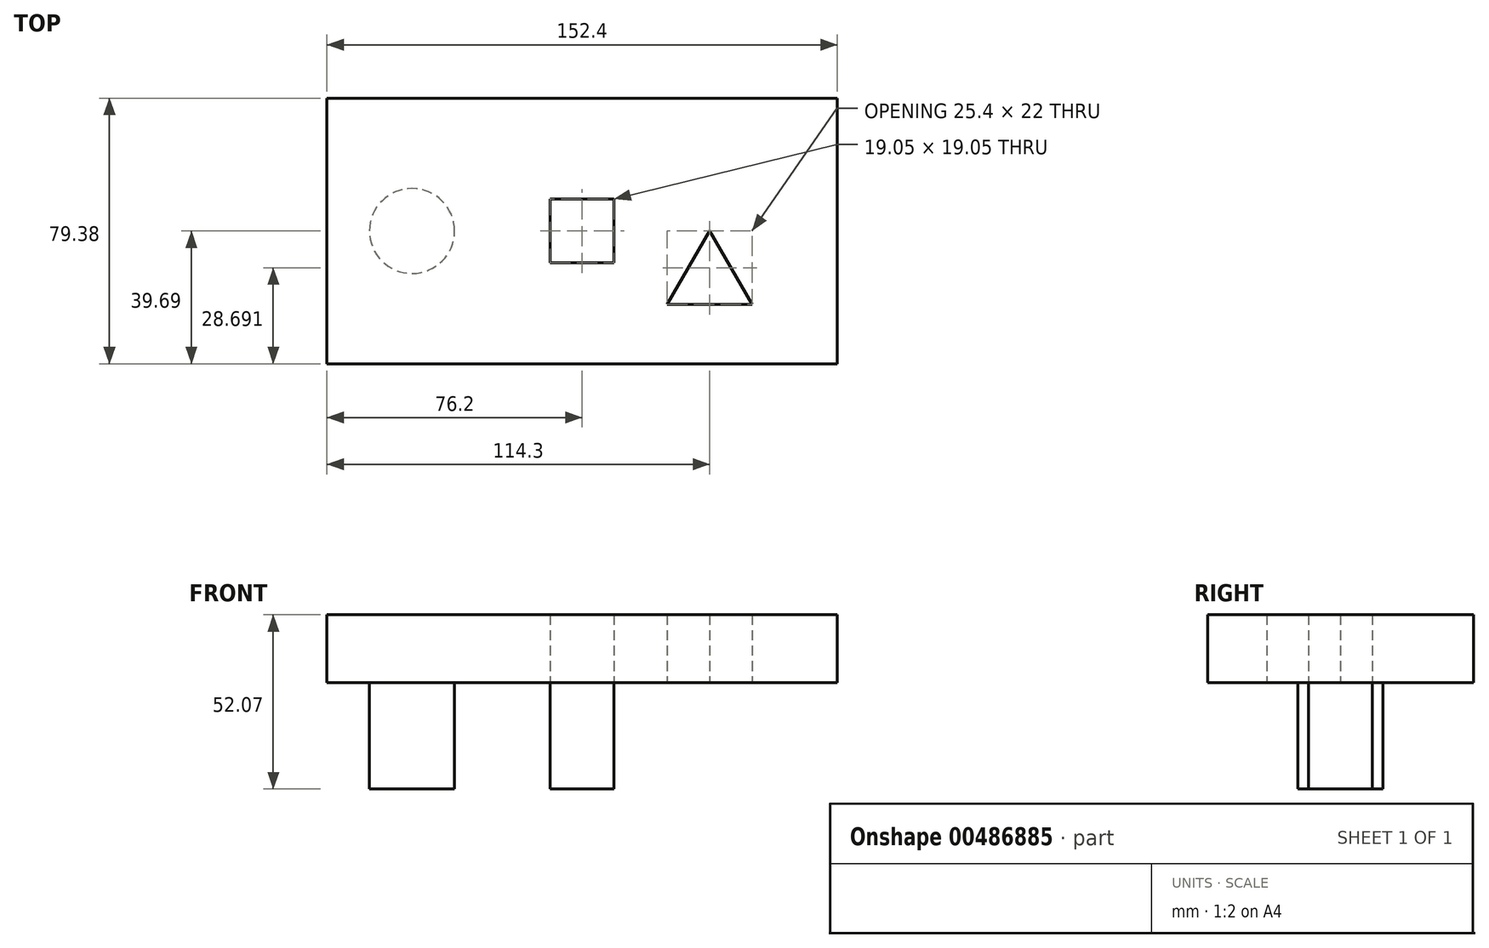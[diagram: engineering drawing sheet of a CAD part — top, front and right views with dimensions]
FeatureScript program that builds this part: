
annotation { "Feature Type Name" : "Feature", "Feature Type Description" : "" }
export const myFeature = defineFeature(function(context is Context, id is Id, definition is map)
    precondition{}
    {
        {
            var Q0;
            Q0=qCreatedBy(makeId("Top.planeOp"),FACE);
            var sketch = newSketch(context, id + "F0", { "sketchPlane" : qUnion([Q0])});
            skPoint(sketch, "E0", {"position": v(-31.75, 0) * mm});
            skLineSegment(sketch, "E1.bottom", {"start": v(-22.22, 9.53) * mm, "end": v(-41.27, 9.53) * mm});
            skLineSegment(sketch, "E1.top", {"start": v(-22.22, -9.52) * mm, "end": v(-41.27, -9.52) * mm});
            skLineSegment(sketch, "E1.left", {"start": v(-22.22, 9.53) * mm, "end": v(-22.22, -9.52) * mm});
            skLineSegment(sketch, "E1.right", {"start": v(-41.27, 9.53) * mm, "end": v(-41.27, -9.52) * mm});
            skCircle(sketch, "E2", {"center": v(-82.55, 0) * mm, "radius": 12.7 * mm});
            skLineSegment(sketch, "E3.bottom", {"start": v(44.45, -39.69) * mm, "end": v(-107.95, -39.69) * mm});
            skLineSegment(sketch, "E3.top", {"start": v(44.45, 39.69) * mm, "end": v(-107.95, 39.69) * mm});
            skLineSegment(sketch, "E3.left", {"start": v(44.45, -39.69) * mm, "end": v(44.45, 39.69) * mm});
            skLineSegment(sketch, "E3.right", {"start": v(-107.95, -39.69) * mm, "end": v(-107.95, 39.69) * mm});
            skPoint(sketch, "E4", {"position": v(44.45, 0) * mm});
            skPoint(sketch, "E5", {"position": v(6.35, 0) * mm});
            skLineSegment(sketch, "E6", {"start": v(6.35, 0) * mm, "end": v(-6.35, -22) * mm});
            skLineSegment(sketch, "E7", {"start": v(-6.35, -22) * mm, "end": v(19.05, -22) * mm});
            skLineSegment(sketch, "E8", {"start": v(19.05, -22) * mm, "end": v(6.35, 0) * mm});
            skSolve(sketch);
        }
        {
            var Q0;
            Q0=makeQuery(id+"F0.imprint","IMPRINT",FACE,{"disambiguationData":[TD([[makeQuery(id+"F0.imprint","IMPRINT",EDGE,{"derivedFrom":sQuery(id+"F0.wireOp",EDGE,"E1.bottom")}),-1.0]])]});
            var Q1;
            Q1=makeQuery(id+"F0.imprint","IMPRINT",FACE,{"disambiguationData":[TD([[makeQuery(id+"F0.imprint","IMPRINT",EDGE,{"derivedFrom":sQuery(id+"F0.wireOp",EDGE,"E2")}),1.0]])]});
            var Q2;
            Q2=makeQuery(id+"F0.imprint","IMPRINT",FACE,{"disambiguationData":[TD([[makeQuery(id+"F0.imprint","IMPRINT",EDGE,{"derivedFrom":sQuery(id+"F0.wireOp",EDGE,"1dAGqZZK-PbFe-BUMY-NSrG-KrEZ7z0RWpoe")}),1.0]])]});
            var Q3;
            Q3=makeQuery(id+"F0.imprint","IMPRINT",FACE,{"disambiguationData":[TD([[makeQuery(id+"F0.imprint","IMPRINT",EDGE,{"derivedFrom":sQuery(id+"F0.wireOp",EDGE,"LygEi8Ur-gzNw-TDgE-Le7G-bf86k6djG2GS")}),1.0]])]});
            var Q4;
            Q4=makeQuery(id+"F0.imprint","IMPRINT",FACE,{"disambiguationData":[TD([[makeQuery(id+"F0.imprint","IMPRINT",EDGE,{"derivedFrom":sQuery(id+"F0.wireOp",EDGE,"tCn7Srsb-gwfL-v9CE-pRFE-bM4LpM3Rr9z0")}),1.0]])]});
            var Q5;
            Q5=makeQuery(id+"F0.imprint","IMPRINT",FACE,{"disambiguationData":[TD([[makeQuery(id+"F0.imprint","IMPRINT",EDGE,{"derivedFrom":sQuery(id+"F0.wireOp",EDGE,"NWhCxObp-BHab-S6VO-F033-pommvVcIhDGg")}),1.0]])]});
            var Q6;
            Q6=makeQuery(id+"F0.imprint","IMPRINT",FACE,{"disambiguationData":[TD([[makeQuery(id+"F0.imprint","IMPRINT",EDGE,{"derivedFrom":sQuery(id+"F0.wireOp",EDGE,"Vu1bnHFe-H9mk-ZCjp-7Mg4-KF9IkP5c8JJK")}),1.0]])]});
            extrude(context, id + "F1", {"entities" : qUnion([Q0, Q1, Q2, Q3, Q4, Q5, Q6]), "depth" : 20.32 * mm});
        }
        {
            var Q0;
            Q0=makeQuery(id+"F0.imprint","IMPRINT",FACE,{"disambiguationData":[TD([[makeQuery(id+"F0.imprint","IMPRINT",EDGE,{"derivedFrom":sQuery(id+"F0.wireOp",EDGE,"E2")}),1.0]])]});
            extrude(context, id + "F2", {"entities" : qUnion([Q0]), "oppositeDirection" : true, "depth" : 31.75 * mm});
        }
        {
            var Q0;
            Q0=makeQuery(id+"F0.imprint","IMPRINT",FACE,{"disambiguationData":[TD([[makeQuery(id+"F0.imprint","IMPRINT",EDGE,{"derivedFrom":sQuery(id+"F0.wireOp",EDGE,"E1.bottom")}),1.0]])]});
            extrude(context, id + "F3", {"entities" : qUnion([Q0]), "oppositeDirection" : true, "depth" : 31.75 * mm});
        }
    });
